# Revit family: Haworth_Compose_Worksurface_Key
name_source: partatom
category: Furniture Systems
revit_build: Autodesk Revit 2018 (Build: 20170223_1515(x64)
units: mm (PartAtom-declared; Revit-internal decimal feet)

## family parameters
Always vertical = Yes
Cut with Voids When Loaded = No
OmniClass Number = 23.40.70.14.64.21
OmniClass Title = Systems Furniture
Part Type = Normal
Room Calculation Point = No
Round Connector Dimension = Use Diameter
Shared = No
Work Plane-Based = No

## types (8) — shared parameters
Actual Height = 29"
Assembly Code = E2020200
Custom Size = No
Description = Haworth Worksurface - Compose Key
Disc Base Support = Yes
Flip-top Location = 4"
Height = 29"
Leg Height = 27 13/16"
Manufacturer = Haworth
Max. Depth = 48"
Max. Height = 42"
Max. Width = 72"
Min. Depth = 30"
Min. Height = 22"
Min. Width = 36"
Min/Max Depth = 30, 36, 42, 48 in.
Min/Max Height = 26-32 in.
Model = WURY
Revision Number = 5
Size = Verify Final Dim. w/ Haworth
Support Column = No
Support Finish = Haworth _ Paint _ Metallic Champagne
Sustainability Info = http://media.haworth.com
Table Thickness = 1 3/16"
URL = www.haworth.com
URL - Product = http://www.haworth.com
Warranty = http://www.haworth.com
Worksurface Edge Finish = Haworth _ Laminate _ Maple H-AE
Worksurface Finish = Haworth _ Laminate _ Maple H-AE

## per-type parameters (varying)
| type | Actual Depth | Actual Width | Depth | Disc Base Radius | Min/Max Width | Width |
| 48w 30d | 30" | 48" | 30" | 10 1/2" | 36, 48 in. | 48" |
| 36w 30d | 30" | 36" | 30" | 10 1/2" | 36, 48 in. | 36" |
| 48w 36d | 36" | 48" | 36" | 10 1/2" | 48, 60, 72 in. | 48" |
| 36w 36d | 36" | 36" | 36" | 10 1/2" | 48, 60, 72 in. | 36" |
| 48w 42d | 42" | 48" | 42" | 13 1/2" | 60, 72 in. | 48" |
| 36w 42d | 42" | 42" | 42" | 13 1/2" | 60, 72 in. | 36" |
| 48w 48d | 48" | 48" | 48" | 13 1/2" | 60, 72 in. | 48" |
| 36w 48d | 48" | 48" | 48" | 13 1/2" | 60, 72 in. | 36" |

## geometry (parser evidence)
native form markers: Sweep x7
no freeform markers — native parametric forms only
